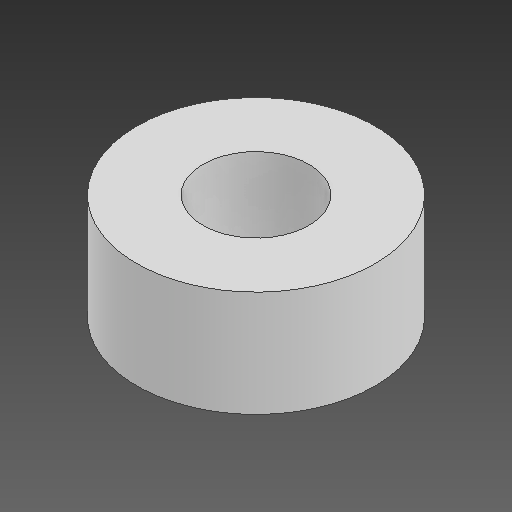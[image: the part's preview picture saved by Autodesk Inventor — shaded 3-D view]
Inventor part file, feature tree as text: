
AUTODESK INVENTOR PART (.ipt)
format: ipt  version: 2021 (Build 250183000, 183)  size: 88,576 bytes
history: native  units: mm
features: extrude x1, sketch x1
ambient origin geometry x8: Origin, YZ Plane, XZ Plane, XY Plane, X Axis, Y Axis, Z Axis, Center Point
bodies: Solid1 (feature_tree)
feature tree (2):
  extrude  "Extrusion1"  Depth=4.0mm
  sketch  "Sketch1"  dims[d0=9.0mm d1=4.0mm d2=4.0mm d3=0.0mm]
